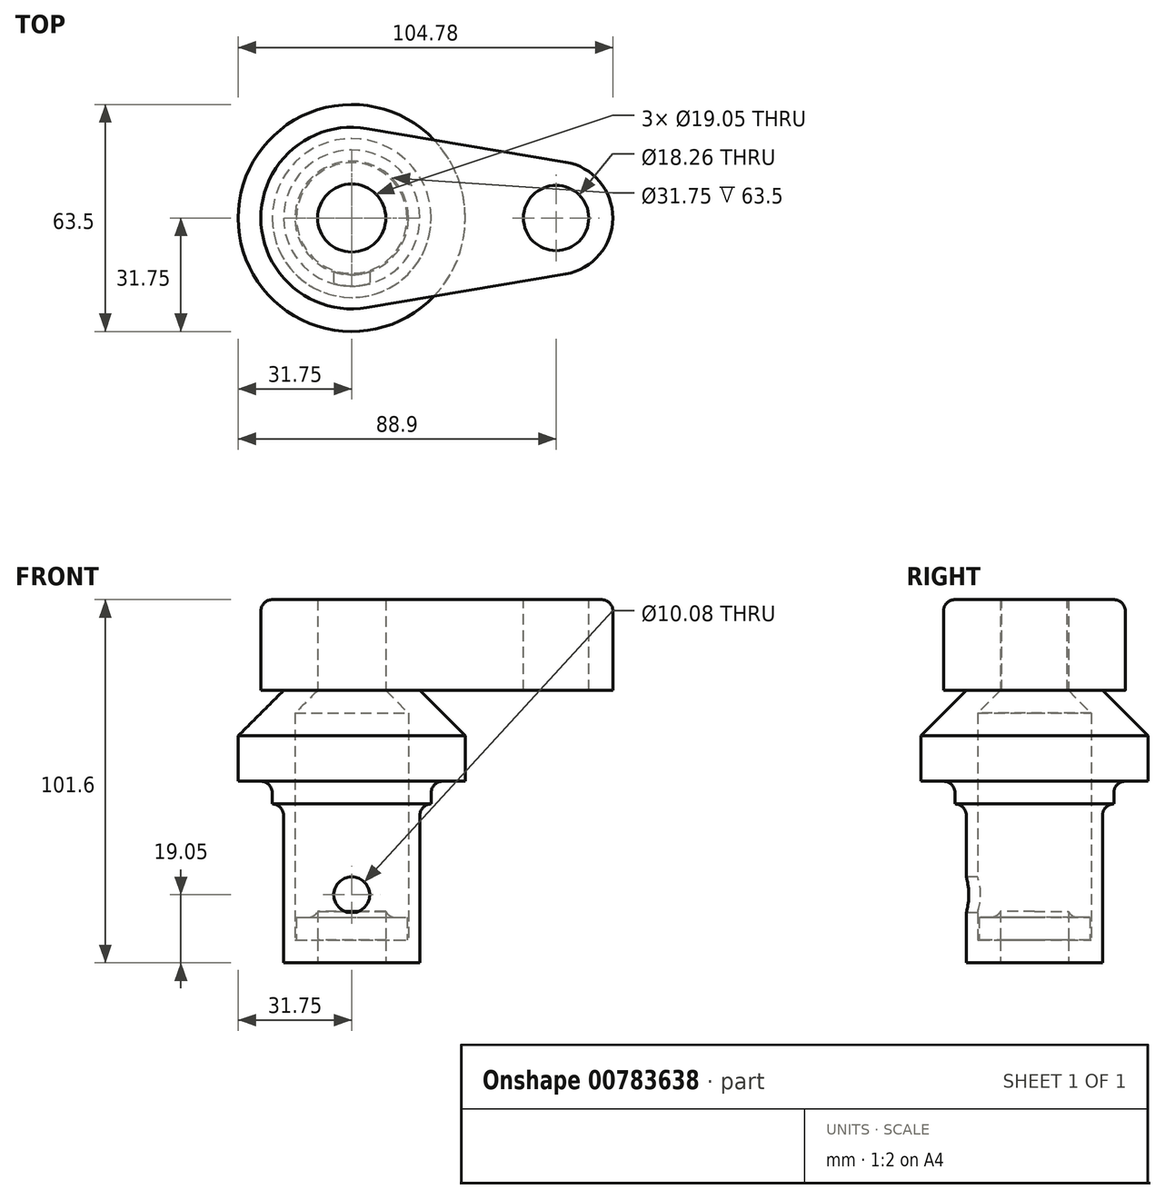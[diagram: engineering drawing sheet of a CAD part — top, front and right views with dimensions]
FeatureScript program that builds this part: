
annotation { "Feature Type Name" : "Feature", "Feature Type Description" : "" }
export const myFeature = defineFeature(function(context is Context, id is Id, definition is map)
    precondition{}
    {
        {
            var Q0;
            Q0=qCreatedBy(makeId("Front.planeOp"),FACE);
            var sketch = newSketch(context, id + "F0", { "sketchPlane" : qUnion([Q0])});
            skLineSegment(sketch, "E0", {"start": v(0, 0) * mm, "end": v(0, 76.2) * mm});
            skLineSegment(sketch, "E1", {"start": v(0, 76.2) * mm, "end": v(19.05, 76.2) * mm});
            skLineSegment(sketch, "E2", {"start": v(19.05, 76.2) * mm, "end": v(31.75, 63.5) * mm});
            skLineSegment(sketch, "E3", {"start": v(31.75, 63.5) * mm, "end": v(31.75, 50.8) * mm});
            skLineSegment(sketch, "E4", {"start": v(31.75, 50.8) * mm, "end": v(22.23, 50.8) * mm});
            skLineSegment(sketch, "E5", {"start": v(22.23, 50.8) * mm, "end": v(22.23, 44.45) * mm});
            skLineSegment(sketch, "E6", {"start": v(22.23, 44.45) * mm, "end": v(19.05, 44.45) * mm});
            skLineSegment(sketch, "E7", {"start": v(19.05, 44.45) * mm, "end": v(19.05, 0) * mm});
            skLineSegment(sketch, "E8", {"start": v(19.05, 0) * mm, "end": v(0, 0) * mm});
            skLineSegment(sketch, "E9", {"start": v(9.53, 76.2) * mm, "end": v(15.88, 69.85) * mm});
            skLineSegment(sketch, "E10", {"start": v(15.88, 69.85) * mm, "end": v(15.88, 6.35) * mm});
            skLineSegment(sketch, "E11", {"start": v(15.88, 6.35) * mm, "end": v(0, 6.35) * mm});
            skLineSegment(sketch, "E12", {"start": v(0, 76.2) * mm, "end": v(0, 93.34) * mm, "construction": true});
            skLineSegment(sketch, "E13", {"start": v(0, 76.2) * mm, "end": v(0, 101.6) * mm});
            skLineSegment(sketch, "E14", {"start": v(0, 101.6) * mm, "end": v(9.13, 101.6) * mm});
            skLineSegment(sketch, "E15", {"start": v(9.13, 101.6) * mm, "end": v(9.13, 12.7) * mm});
            skLineSegment(sketch, "E16", {"start": v(9.13, 12.7) * mm, "end": v(15.48, 12.7) * mm});
            skLineSegment(sketch, "E17", {"start": v(15.48, 12.7) * mm, "end": v(15.48, 6.35) * mm});
            skSolve(sketch);
        }
        {
            var Q0;
            {var subQ4=sQuery(id+"F0.wireOp",EDGE,"E2");Q0=makeQuery(id+"F0.imprint","IMPRINT",FACE,{"disambiguationData":[TD([[makeQuery(id+"F0.imprint","IMPRINT",EDGE,{"derivedFrom":subQ4}),-1.0]])]});}
            var Q1;
            Q1=sQuery(id+"F0.wireOp",EDGE,"E0");
            revolve(context, id + "F1", {"surfaceOperationType" : NewSurfaceOperationType.NEW, "entities" : qUnion([Q0]), "axis" : qUnion([Q1]), "revolveType" : RevolveType.FULL});
        }
        {
            var Q0;
            {var subQ0=sQuery(id+"F0.wireOp",EDGE,"E13");Q0=makeQuery(id+"F0.imprint","IMPRINT",FACE,{"disambiguationData":[TD([[makeQuery(id+"F0.imprint","IMPRINT",EDGE,{"derivedFrom":subQ0}),-1.0]])]});}
            var Q1;
            {var subQ0=sQuery(id+"F0.wireOp",EDGE,"E16");Q1=makeQuery(id+"F0.imprint","IMPRINT",FACE,{"disambiguationData":[TD([[makeQuery(id+"F0.imprint","IMPRINT",EDGE,{"derivedFrom":subQ0}),-1.0]])]});}
            var Q2;
            Q2=sQuery(id+"F0.wireOp",EDGE,"E13");
            revolve(context, id + "F2", {"surfaceOperationType" : NewSurfaceOperationType.NEW, "entities" : qUnion([Q0, Q1]), "axis" : qUnion([Q2]), "revolveType" : RevolveType.FULL});
        }
        {
            var Q0;
            Q0=makeQuery(id+"F2.opRevolve","SWEPT_FACE",FACE,{"disambiguationData":[OSD([sQuery(id+"F0.wireOp",EDGE,"E14")])]});
            var sketch = newSketch(context, id + "F3", { "sketchPlane" : qUnion([Q0])});
            skCircle(sketch, "E18", {"center": v(0, 0) * mm, "radius": 25.4 * mm});
            skCircle(sketch, "E19", {"center": v(57.15, 0) * mm, "radius": 15.88 * mm});
            skLineSegment(sketch, "E20", {"start": v(59.8, 15.65) * mm, "end": v(4.23, 25.04) * mm});
            skLineSegment(sketch, "E21", {"start": v(59.8, -15.65) * mm, "end": v(4.23, -25.04) * mm});
            skCircle(sketch, "E22.0", {"center": v(0, 0) * mm, "radius": 9.13 * mm});
            skCircle(sketch, "E23", {"center": v(57.15, 0) * mm, "radius": 9.13 * mm});
            skSolve(sketch);
        }
        {
            var Q0;
            Q0 = qSketchRegion(id + "F3", true);
            var Q1;
            Q1=makeQuery(id+"F1.opRevolve","SWEPT_FACE",FACE,{"disambiguationData":[OSD([sQuery(id+"F0.wireOp",EDGE,"E1")])]});
            extrude(context, id + "F4", {"entities" : qUnion([Q0]), "oppositeDirection" : true, "depth" : 25.4 * mm, "endBoundEntityFace" : qUnion([Q1]), "offsetDistance" : 1 / 812.8 * mm});
        }
        {
            var Q0;
            Q0=qCreatedBy(makeId("Front.planeOp"),FACE);
            var sketch = newSketch(context, id + "F5", { "sketchPlane" : qUnion([Q0])});
            skPoint(sketch, "E24", {"position": v(0, 19.05) * mm});
            skSolve(sketch);
        }
        {
            var Q0;
            Q0=sQuery(id+"F5.wireOp",VERTEX,"E24");
            var Q1;
            Q1=makeQuery(id+"F1.opRevolve","SWEPT_BODY",BODY,{"disambiguationData":[OSD([sQuery(id+"F0.wireOp",EDGE,"E0"),sQuery(id+"F0.wireOp",EDGE,"E1"),sQuery(id+"F0.wireOp",EDGE,"E2"),sQuery(id+"F0.wireOp",EDGE,"E3"),sQuery(id+"F0.wireOp",EDGE,"E4"),sQuery(id+"F0.wireOp",EDGE,"E5"),sQuery(id+"F0.wireOp",EDGE,"E6"),sQuery(id+"F0.wireOp",EDGE,"E7"),sQuery(id+"F0.wireOp",EDGE,"E8"),sQuery(id+"F0.wireOp",EDGE,"E9"),sQuery(id+"F0.wireOp",EDGE,"E10"),sQuery(id+"F0.wireOp",EDGE,"E11")])]});
            hole(context, id + "F6", {"style" : HoleStyle.SIMPLE, "endStyle" : HoleEndStyle.THROUGH, "oppositeDirection" : true, "standardTappedOrClearance" : lookupTablePath({ "standard" : "ANSI", "fit" : "Normal (ASME)", "size" : "3/8", "type" : "Clearance" }), "standardBlindInLast" : lookupTablePath({ "fit" : "Free", "standard" : "ANSI", "size" : "3/8", "type" : "Clearance" }), "holeDiameter" : 10.08 * mm, "majorDiameter" : 6.35 * mm, "tappedDepth" : 14.3 * mm, "tapClearance" : 3, "locations" : qUnion([Q0]), "scope" : qUnion([Q1]), "startStyle" : HoleStartStyle.PART});
        }
        {
            var Q0;
            Q0=makeQuery(id+"F4.opExtrude","CAP_EDGE",EDGE,{"disambiguationData":[OSD([sQuery(id+"F3.wireOp",EDGE,"E20")])],"isStart":true});
            var Q1;
            Q1=makeQuery(id+"F1.opRevolve","SWEPT_EDGE",EDGE,{"disambiguationData":[OSD([sQuery(id+"F0.wireOp",EDGE,"E4"),sQuery(id+"F0.wireOp",EDGE,"E5")])]});
            var Q2;
            Q2=makeQuery(id+"F1.opRevolve","SWEPT_EDGE",EDGE,{"disambiguationData":[OSD([sQuery(id+"F0.wireOp",EDGE,"E6"),sQuery(id+"F0.wireOp",EDGE,"E7")])]});
            var Q3;
            Q3=makeQuery(id+"F2.opRevolve","SWEPT_EDGE",EDGE,{"disambiguationData":[OSD([sQuery(id+"F0.wireOp",EDGE,"E15"),sQuery(id+"F0.wireOp",EDGE,"E16")])]});
            fillet(context, id + "F7", {"entities" : qUnion([Q0, Q1, Q2, Q3]), "radius" : 3.17 * mm, "tangentPropagation" : true, "allowEdgeOverflow" : false});
        }
        {
            var Q0;
            Q0=makeQuery(id+"F1.opRevolve","SWEPT_FACE",FACE,{"disambiguationData":[OSD([sQuery(id+"F0.wireOp",EDGE,"E8")])]});
            var sketch = newSketch(context, id + "F8", { "sketchPlane" : qUnion([Q0])});
            skCircle(sketch, "E25", {"center": v(0, 0) * mm, "radius": 9.53 * mm});
            skSolve(sketch);
        }
        {
            var Q0;
            Q0 = qSketchRegion(id + "F8", true);
            extrude(context, id + "F9", {"entities" : qUnion([Q0]), "operationType" : NewBodyOperationType.REMOVE, "endBound" : BoundingType.THROUGH_ALL, "oppositeDirection" : true, "depth" : 25.4 * mm, "offsetDistance" : 25.4 * mm});
        }
    });
